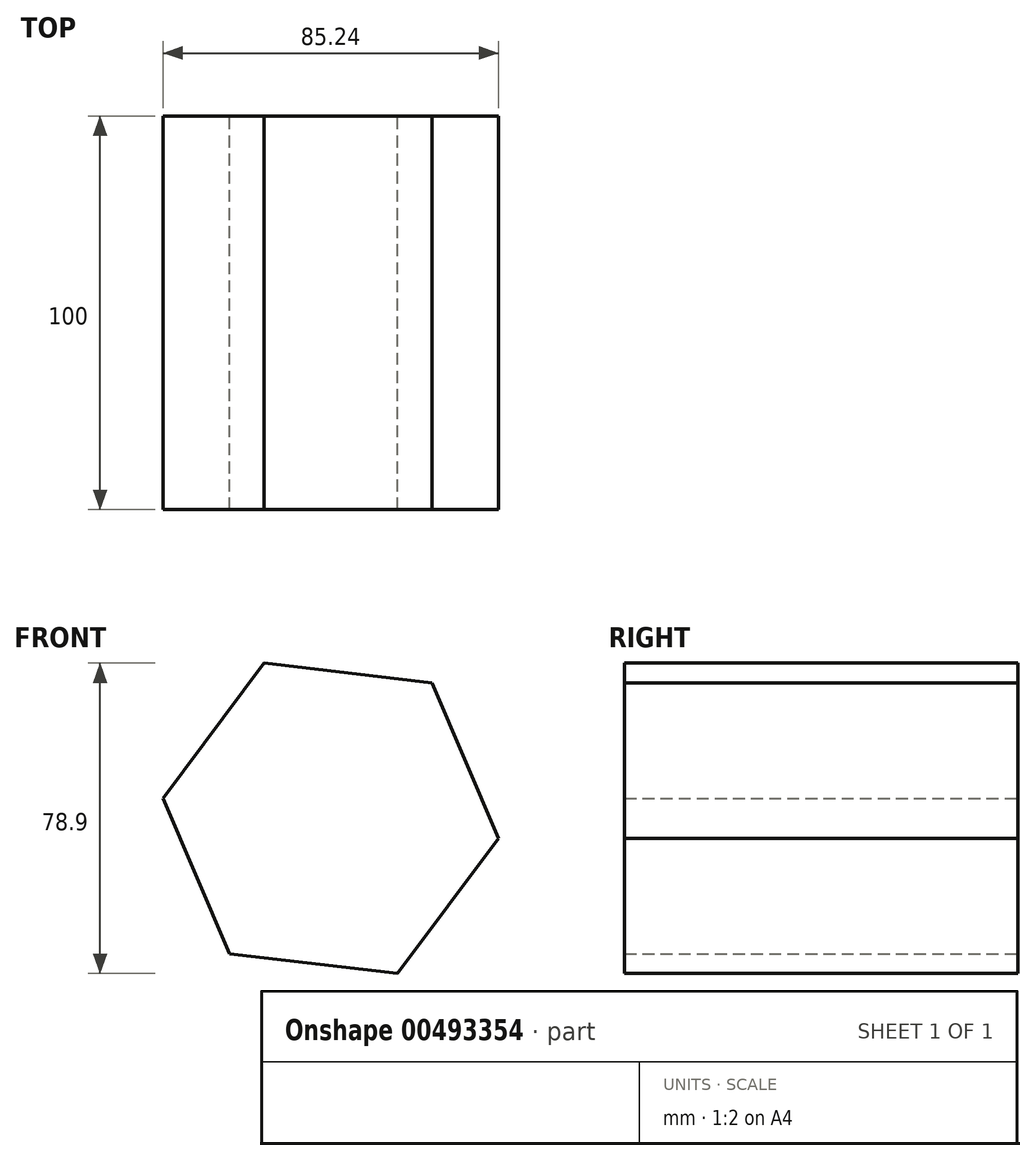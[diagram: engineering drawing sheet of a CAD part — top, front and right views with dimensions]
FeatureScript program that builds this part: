
annotation { "Feature Type Name" : "Feature", "Feature Type Description" : "" }
export const myFeature = defineFeature(function(context is Context, id is Id, definition is map)
    precondition{}
    {
        {
            var Q0;
            Q0=qCreatedBy(makeId("Front.planeOp"),FACE);
            var sketch = newSketch(context, id + "F0", { "sketchPlane" : qUnion([Q0])});
            skCircle(sketch, "E0.cCircle", {"center": v(0, 0) * mm, "radius": 42.92 * mm, "construction": true});
            skLineSegment(sketch, "E0.0", {"start": v(-16.93, 39.45) * mm, "end": v(25.7, 34.38) * mm});
            skLineSegment(sketch, "E0.1", {"start": v(25.7, 34.38) * mm, "end": v(42.62, -5.06) * mm});
            skLineSegment(sketch, "E0.2", {"start": v(42.62, -5.06) * mm, "end": v(16.93, -39.45) * mm});
            skLineSegment(sketch, "E0.3", {"start": v(16.93, -39.45) * mm, "end": v(-25.7, -34.38) * mm});
            skLineSegment(sketch, "E0.4", {"start": v(-25.7, -34.38) * mm, "end": v(-42.62, 5.06) * mm});
            skLineSegment(sketch, "E0.5", {"start": v(-42.62, 5.06) * mm, "end": v(-16.93, 39.45) * mm});
            skSolve(sketch);
        }
        {
            var Q0;
            Q0 = qSketchRegion(id + "F0", true);
            extrude(context, id + "F1", {"entities" : qUnion([Q0]), "endBound" : BoundingType.SYMMETRIC, "depth" : 100 * mm});
        }
    });
